# Revit family: БАС-150.4
name_source: partatom
category: Устройства вызова и оповещения
revit_build: Autodesk Revit 2017 (Build: 20160225_1515(x64)
units: mm (PartAtom-declared; Revit-internal decimal feet)

## family parameters
Всегда вертикально = Да
На основе рабочей плоскости = Нет
Общий = Нет
При загрузке вырезать с полостями = Нет
Размер круглого соединителя = Использовать диаметр
Сохранять ориентацию аннотаций = Нет
Тип детали = Нормальный
Точка расчета площади = Нет

## types (1)
- БАС-150.4
    URL = http://rechor.ru
    Высота = 305 мм
    Глубина = 125 мм
    Длина = 405 мм
    Зон оповещения = до 4 зон (до 36 зон в комплексе)
    Изготовитель = СОУЭ 'Речор'
    Источник резервоного питания = встроенный
    Материал = Сталь, окрашенная, темно-серая, матовая
    Микрофон-тангента = в комплекте
    Мощность = 200 В·А
    Мощность в режиме трансляции звуковых сигналов = Не более 200.00 В·А
    Номинальное значение входного сопротивления для линейных входов = 600 Ом
    Описание = Центральный блок системы РЕЧОР-М. Мощность 150Вт, до 4 программируемых сообщений, микрофон-тангента, резервный аккумулятор, 4 зоны коммутации.
    Сообщений трансляции = до 8 программируемых сообщений
    Число входов ШЛ для подключия к устройству = 4
